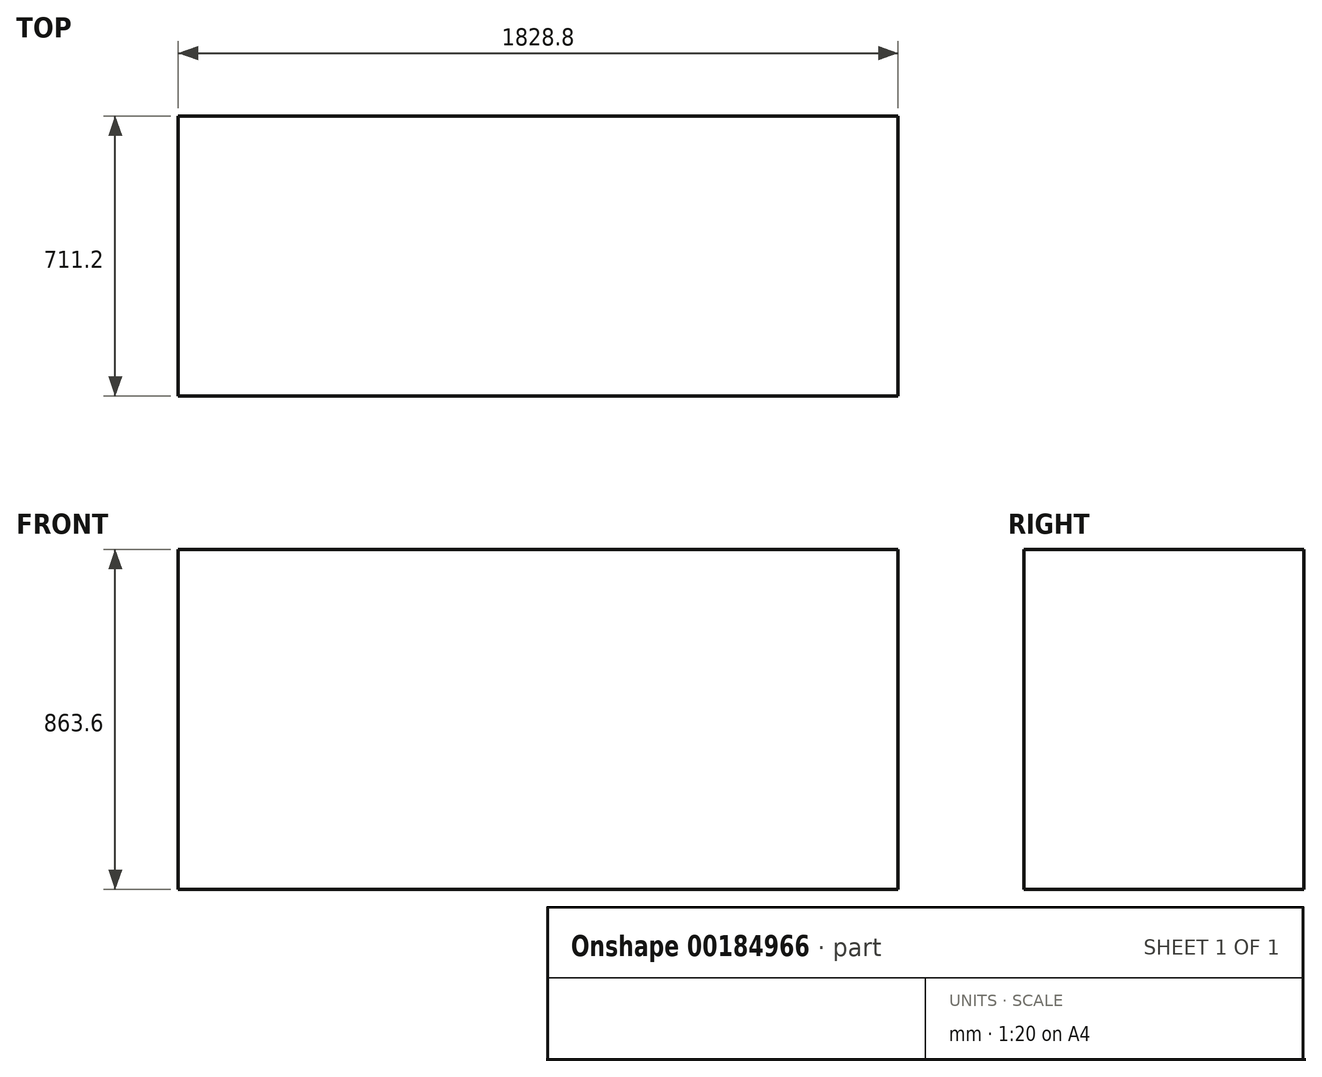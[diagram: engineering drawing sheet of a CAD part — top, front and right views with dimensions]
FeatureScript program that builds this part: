
annotation { "Feature Type Name" : "Feature", "Feature Type Description" : "" }
export const myFeature = defineFeature(function(context is Context, id is Id, definition is map)
    precondition{}
    {
        {
            var Q0;
            Q0=qCreatedBy(makeId("Top.planeOp"),FACE);
            var sketch = newSketch(context, id + "F0", { "sketchPlane" : qUnion([Q0])});
            skLineSegment(sketch, "E0.bottom", {"start": v(914.4, 355.6) * mm, "end": v(-914.4, 355.6) * mm});
            skLineSegment(sketch, "E0.top", {"start": v(914.4, -355.6) * mm, "end": v(-914.4, -355.6) * mm});
            skLineSegment(sketch, "E0.left", {"start": v(914.4, 355.6) * mm, "end": v(914.4, -355.6) * mm});
            skLineSegment(sketch, "E0.right", {"start": v(-914.4, 355.6) * mm, "end": v(-914.4, -355.6) * mm});
            skPoint(sketch, "E0.middle", {"position": v(0, 0) * mm});
            skSolve(sketch);
        }
        {
            var Q0;
            Q0=makeQuery(id+"F0.imprint","IMPRINT",FACE,{"disambiguationData":[TD([[makeQuery(id+"F0.imprint","IMPRINT",EDGE,{"derivedFrom":sQuery(id+"F0.wireOp",EDGE,"E0.bottom")}),1.0]])]});
            extrude(context, id + "F1", {"entities" : qUnion([Q0]), "depth" : 863.6 * mm});
        }
    });
